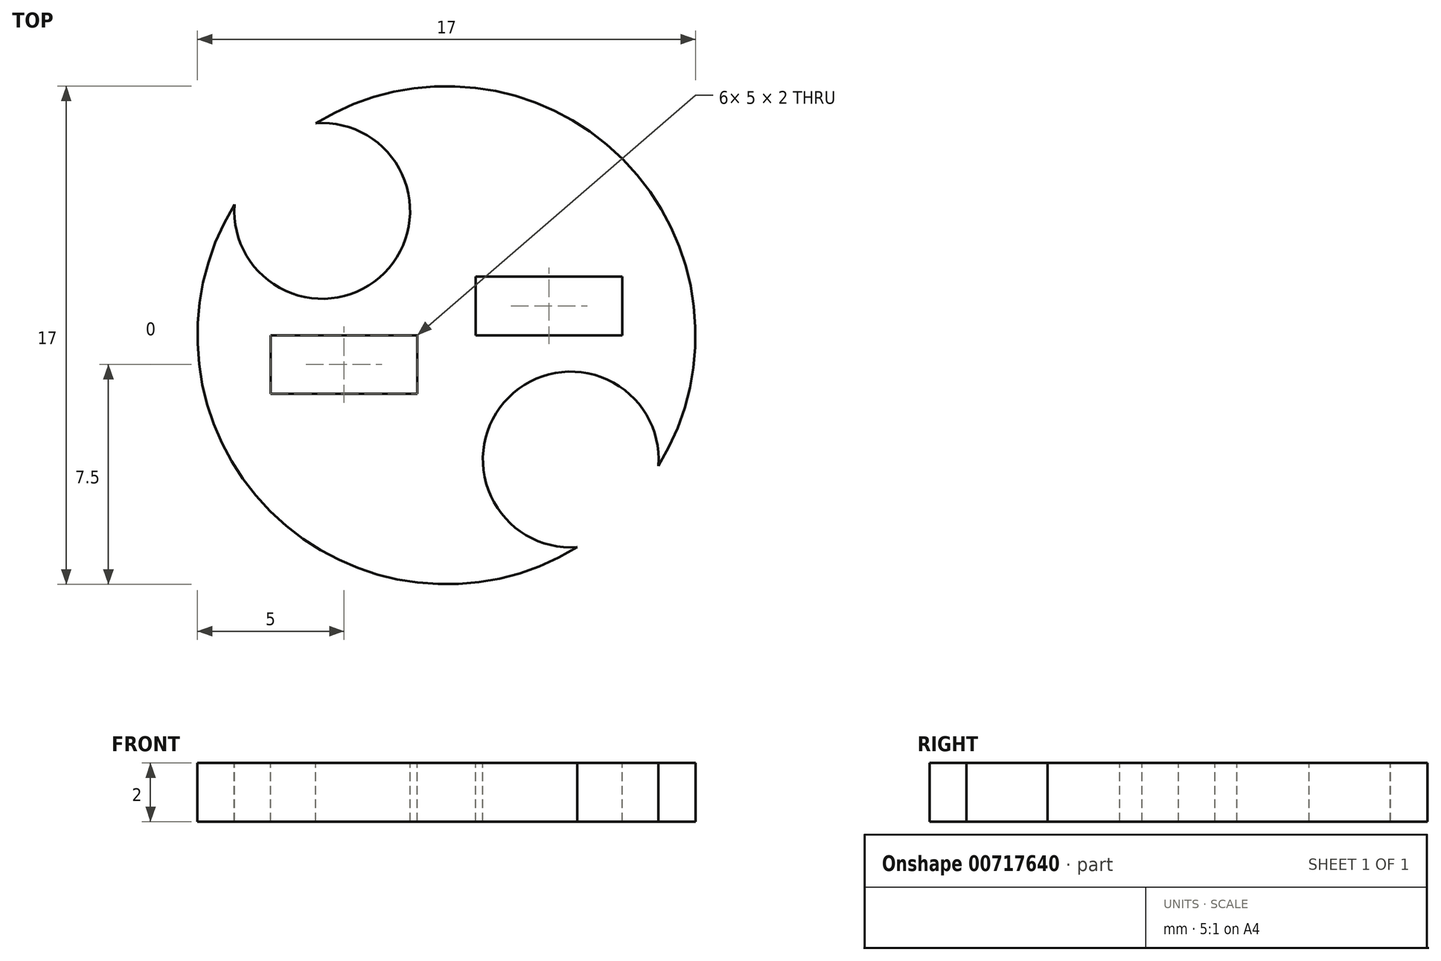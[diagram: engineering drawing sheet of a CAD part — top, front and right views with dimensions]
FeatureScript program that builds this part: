
annotation { "Feature Type Name" : "Feature", "Feature Type Description" : "" }
export const myFeature = defineFeature(function(context is Context, id is Id, definition is map)
    precondition{}
    {
        {
            var Q0;
            Q0=qCreatedBy(makeId("Top.planeOp"),FACE);
            var sketch = newSketch(context, id + "F0", { "sketchPlane" : qUnion([Q0])});
            skCircle(sketch, "E0", {"center": v(0, 0) * mm, "radius": 8.5 * mm});
            skSolve(sketch);
        }
        {
            var Q0;
            Q0=makeQuery(id+"F0.imprint","IMPRINT",FACE,{"disambiguationData":[TD([[makeQuery(id+"F0.imprint","IMPRINT",EDGE,{"derivedFrom":sQuery(id+"F0.wireOp",EDGE,"E0")}),1.0]])]});
            extrude(context, id + "F1", {"entities" : qUnion([Q0]), "oppositeDirection" : true, "depth" : 2 * mm, "offsetDistance" : 25 * mm});
        }
        {
            var Q0;
            Q0=makeQuery(id+"F1.opExtrude","CAP_FACE",FACE,{"disambiguationData":[OSD([sQuery(id+"F0.wireOp",EDGE,"E0")])],"isStart":true});
            var sketch = newSketch(context, id + "F2", { "sketchPlane" : qUnion([Q0])});
            skLineSegment(sketch, "E1", {"start": v(0, 0) * mm, "end": v(6.01, -6.01) * mm});
            skCircle(sketch, "E2", {"center": v(4.24, -4.24) * mm, "radius": 3 * mm});
            skLineSegment(sketch, "E3", {"start": v(0, 0) * mm, "end": v(-6.01, 6.01) * mm});
            skCircle(sketch, "E4", {"center": v(-4.24, 4.24) * mm, "radius": 3 * mm});
            skSolve(sketch);
        }
        {
            var Q0;
            Q0=sQuery(id+"F2.wireOp",VERTEX,"E2.center");
            var Q1;
            Q1=sQuery(id+"F2.wireOp",VERTEX,"E4.center");
            var Q2;
            Q2=makeQuery(id+"F1.opExtrude","SWEPT_BODY",BODY,{"disambiguationData":[OSD([sQuery(id+"F0.wireOp",EDGE,"E0")])]});
            hole(context, id + "F3", {"style" : HoleStyle.SIMPLE, "endStyle" : HoleEndStyle.THROUGH, "holeDiameter" : 6 * mm, "majorDiameter" : 5 * mm, "isTappedThrough" : true, "tappedDepth" : 12 * mm, "tapClearance" : 3, "locations" : qUnion([Q0, Q1]), "scope" : qUnion([Q2])});
        }
        {
            var Q0;
            Q0=makeQuery(id+"F1.opExtrude","CAP_FACE",FACE,{"disambiguationData":[OSD([sQuery(id+"F0.wireOp",EDGE,"E0")])],"isStart":true});
            var sketch = newSketch(context, id + "F4", { "sketchPlane" : qUnion([Q0])});
            skLineSegment(sketch, "E5.bottom", {"start": v(1, 2) * mm, "end": v(6, 2) * mm});
            skLineSegment(sketch, "E5.top", {"start": v(1, 0) * mm, "end": v(6, 0) * mm});
            skLineSegment(sketch, "E5.left", {"start": v(1, 2) * mm, "end": v(1, 0) * mm});
            skLineSegment(sketch, "E5.right", {"start": v(6, 2) * mm, "end": v(6, 0) * mm});
            skLineSegment(sketch, "E6.bottom", {"start": v(-1, 0) * mm, "end": v(-6, 0) * mm});
            skLineSegment(sketch, "E6.top", {"start": v(-1, -2) * mm, "end": v(-6, -2) * mm});
            skLineSegment(sketch, "E6.left", {"start": v(-1, 0) * mm, "end": v(-1, -2) * mm});
            skLineSegment(sketch, "E6.right", {"start": v(-6, 0) * mm, "end": v(-6, -2) * mm});
            skSolve(sketch);
        }
        {
            var Q0;
            Q0=makeQuery(id+"F4.imprint","IMPRINT",FACE,{"disambiguationData":[TD([[makeQuery(id+"F4.imprint","IMPRINT",EDGE,{"derivedFrom":sQuery(id+"F4.wireOp",EDGE,"E6.bottom")}),1.0]])]});
            var Q1;
            Q1=makeQuery(id+"F4.imprint","IMPRINT",FACE,{"disambiguationData":[TD([[makeQuery(id+"F4.imprint","IMPRINT",EDGE,{"derivedFrom":sQuery(id+"F4.wireOp",EDGE,"E5.bottom")}),-1.0]])]});
            extrude(context, id + "F5", {"entities" : qUnion([Q0, Q1]), "operationType" : NewBodyOperationType.REMOVE, "endBound" : BoundingType.THROUGH_ALL, "oppositeDirection" : true, "depth" : 25 * mm, "offsetDistance" : 25 * mm});
        }
    });
